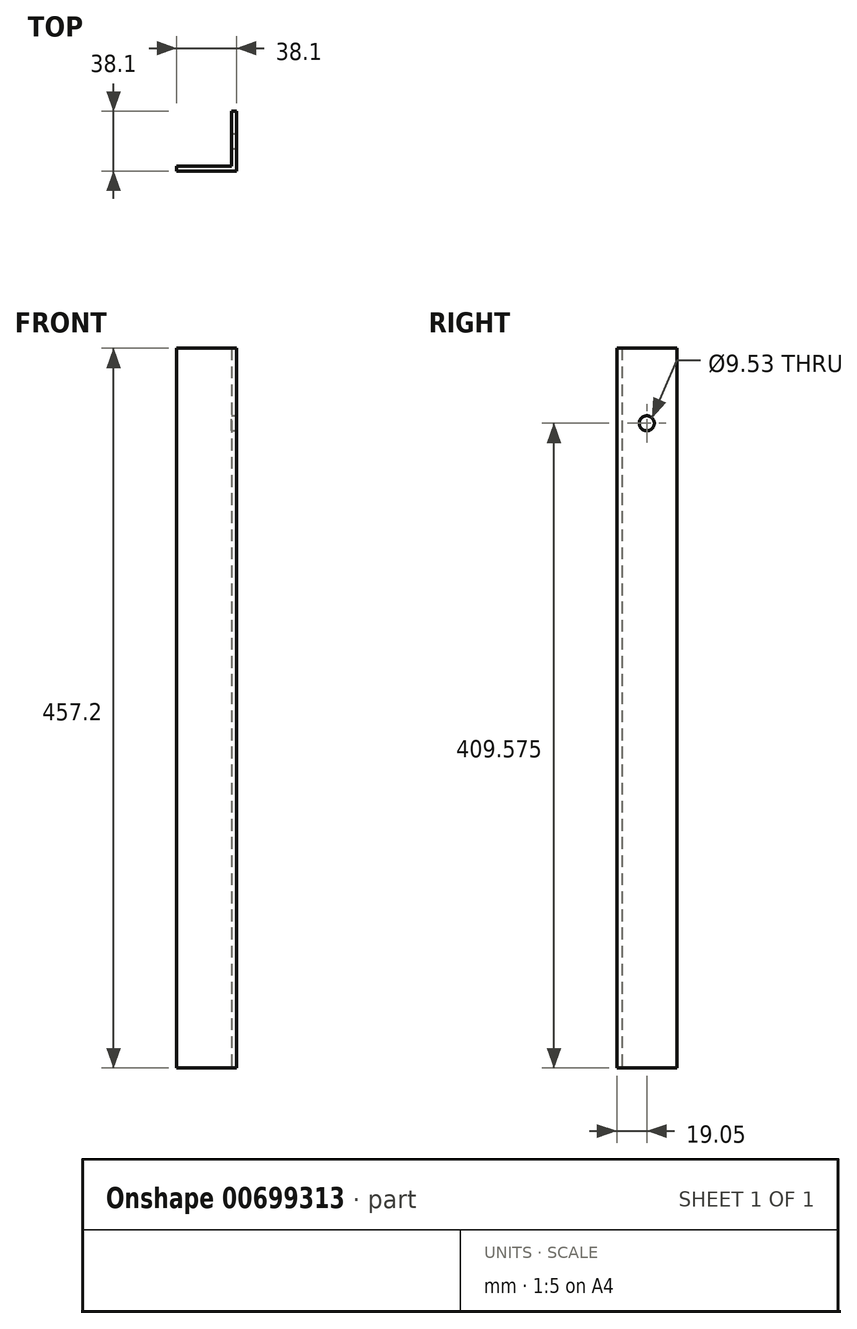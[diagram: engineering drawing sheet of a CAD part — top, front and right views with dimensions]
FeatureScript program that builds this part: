
annotation { "Feature Type Name" : "Feature", "Feature Type Description" : "" }
export const myFeature = defineFeature(function(context is Context, id is Id, definition is map)
    precondition{}
    {
        {
            var Q0;
            Q0=qCreatedBy(makeId("Top.planeOp"),FACE);
            var sketch = newSketch(context, id + "F0", { "sketchPlane" : qUnion([Q0])});
            skLineSegment(sketch, "E0", {"start": v(0, 0) * mm, "end": v(38.1, 0) * mm});
            skLineSegment(sketch, "E1", {"start": v(38.1, 0) * mm, "end": v(38.1, 38.1) * mm});
            skLineSegment(sketch, "E2", {"start": v(38.1, 38.1) * mm, "end": v(34.93, 38.1) * mm});
            skLineSegment(sketch, "E3", {"start": v(34.93, 38.1) * mm, "end": v(34.93, 3.18) * mm});
            skLineSegment(sketch, "E4", {"start": v(34.93, 3.18) * mm, "end": v(0, 3.18) * mm});
            skLineSegment(sketch, "E5", {"start": v(0, 3.18) * mm, "end": v(0, 0) * mm});
            skSolve(sketch);
        }
        {
            var Q0;
            Q0=makeQuery(id+"F0.imprint","IMPRINT",FACE,{"disambiguationData":[TD([[makeQuery(id+"F0.imprint","IMPRINT",EDGE,{"derivedFrom":sQuery(id+"F0.wireOp",EDGE,"E0")}),1.0]])]});
            extrude(context, id + "F1", {"entities" : qUnion([Q0]), "depth" : 457.2 * mm, "offsetDistance" : 25.4 * mm});
        }
        {
            var Q0;
            Q0=makeQuery(id+"F1.opExtrude","SWEPT_FACE",FACE,{"disambiguationData":[OSD([sQuery(id+"F0.wireOp",EDGE,"E1")])]});
            var sketch = newSketch(context, id + "F2", { "sketchPlane" : qUnion([Q0])});
            skCircle(sketch, "E6", {"center": v(19.05, 409.58) * mm, "radius": 4.76 * mm});
            skPoint(sketch, "E6.centerSnap0", {"position": v(19.05, 457.2) * mm});
            skSolve(sketch);
        }
        {
            var Q0;
            Q0=makeQuery(id+"F2.imprint","IMPRINT",FACE,{"disambiguationData":[TD([[makeQuery(id+"F2.imprint","IMPRINT",EDGE,{"derivedFrom":sQuery(id+"F2.wireOp",EDGE,"E6")}),1.0]])]});
            extrude(context, id + "F3", {"entities" : qUnion([Q0]), "operationType" : NewBodyOperationType.REMOVE, "endBound" : BoundingType.THROUGH_ALL, "oppositeDirection" : true, "depth" : 25.4 * mm, "offsetDistance" : 25.4 * mm});
        }
    });
